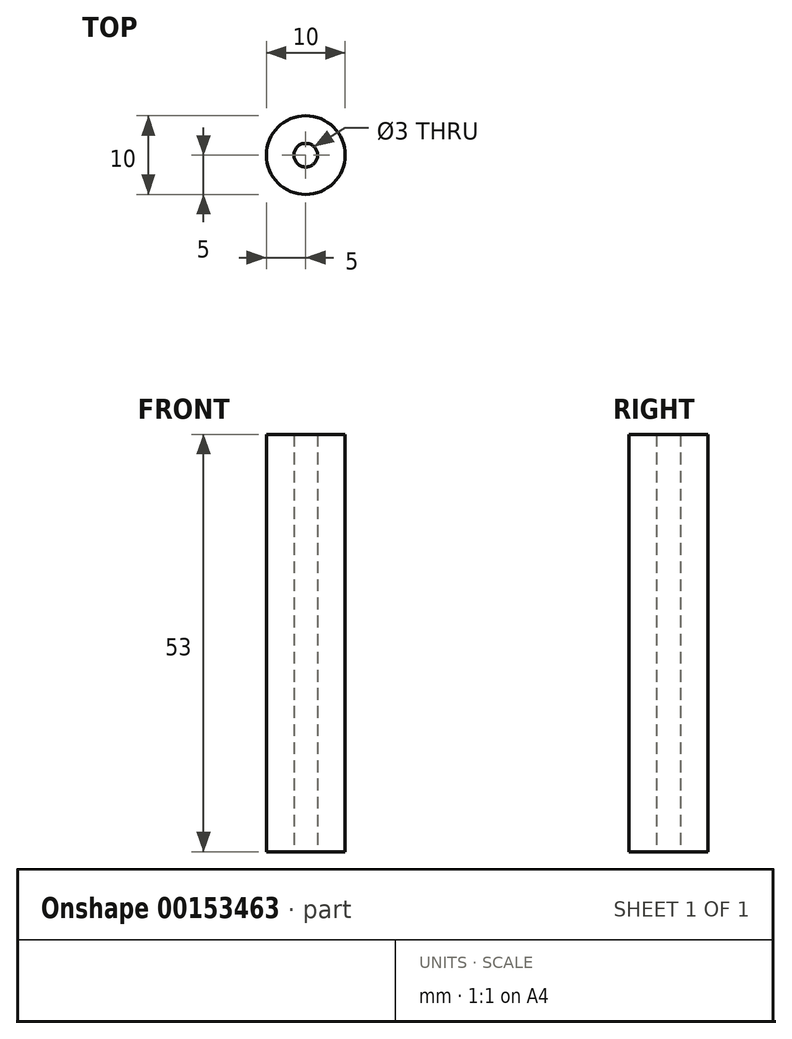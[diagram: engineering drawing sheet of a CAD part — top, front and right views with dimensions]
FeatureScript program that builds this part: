
annotation { "Feature Type Name" : "Feature", "Feature Type Description" : "" }
export const myFeature = defineFeature(function(context is Context, id is Id, definition is map)
    precondition{}
    {
        {
            var Q0;
            Q0=qCreatedBy(makeId("Top.planeOp"),FACE);
            var sketch = newSketch(context, id + "F0", { "sketchPlane" : qUnion([Q0])});
            skCircle(sketch, "E0", {"center": v(0, 0) * mm, "radius": 5 * mm});
            skCircle(sketch, "E1", {"center": v(0, 0) * mm, "radius": 1.5 * mm});
            skSolve(sketch);
        }
        {
            var Q0;
            Q0 = qSketchRegion(id + "F0", true);
            extrude(context, id + "F1", {"entities" : qUnion([Q0]), "depth" : 53 * mm});
        }
    });
